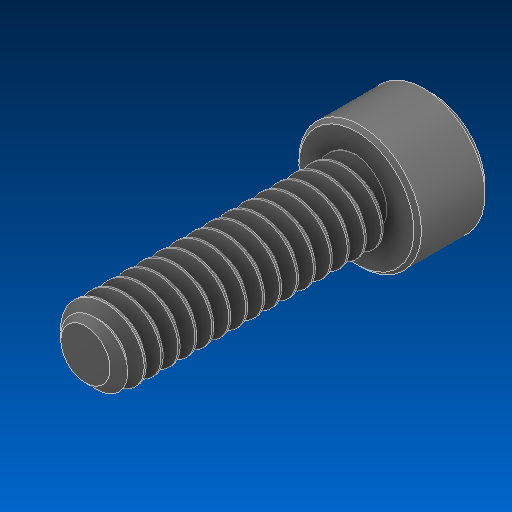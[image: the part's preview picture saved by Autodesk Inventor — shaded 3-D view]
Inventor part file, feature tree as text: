
AUTODESK INVENTOR PART (.ipt)
format: ipt  version: 2022.2 (Build 262287000, 287)  size: 657,920 bytes
history: native  units: in
note: dims shown in document units (in); Inventor stores cm internally (conversion verified against a paired STEP export)
features: chamfer x1
ambient origin geometry x8: Origin, YZ Plane, XZ Plane, XY Plane, X Axis, Y Axis, Z Axis, Center Point
bodies: Solid1 (feature_tree)
feature tree (1):
  chamfer  "Chamfer2"  [1 undecoded]
note: 1 required parameter value undecoded (feature->parameter linkage not recoverable at this tier; creation-order binding heuristic only, values carry confidence <= 0.55)
